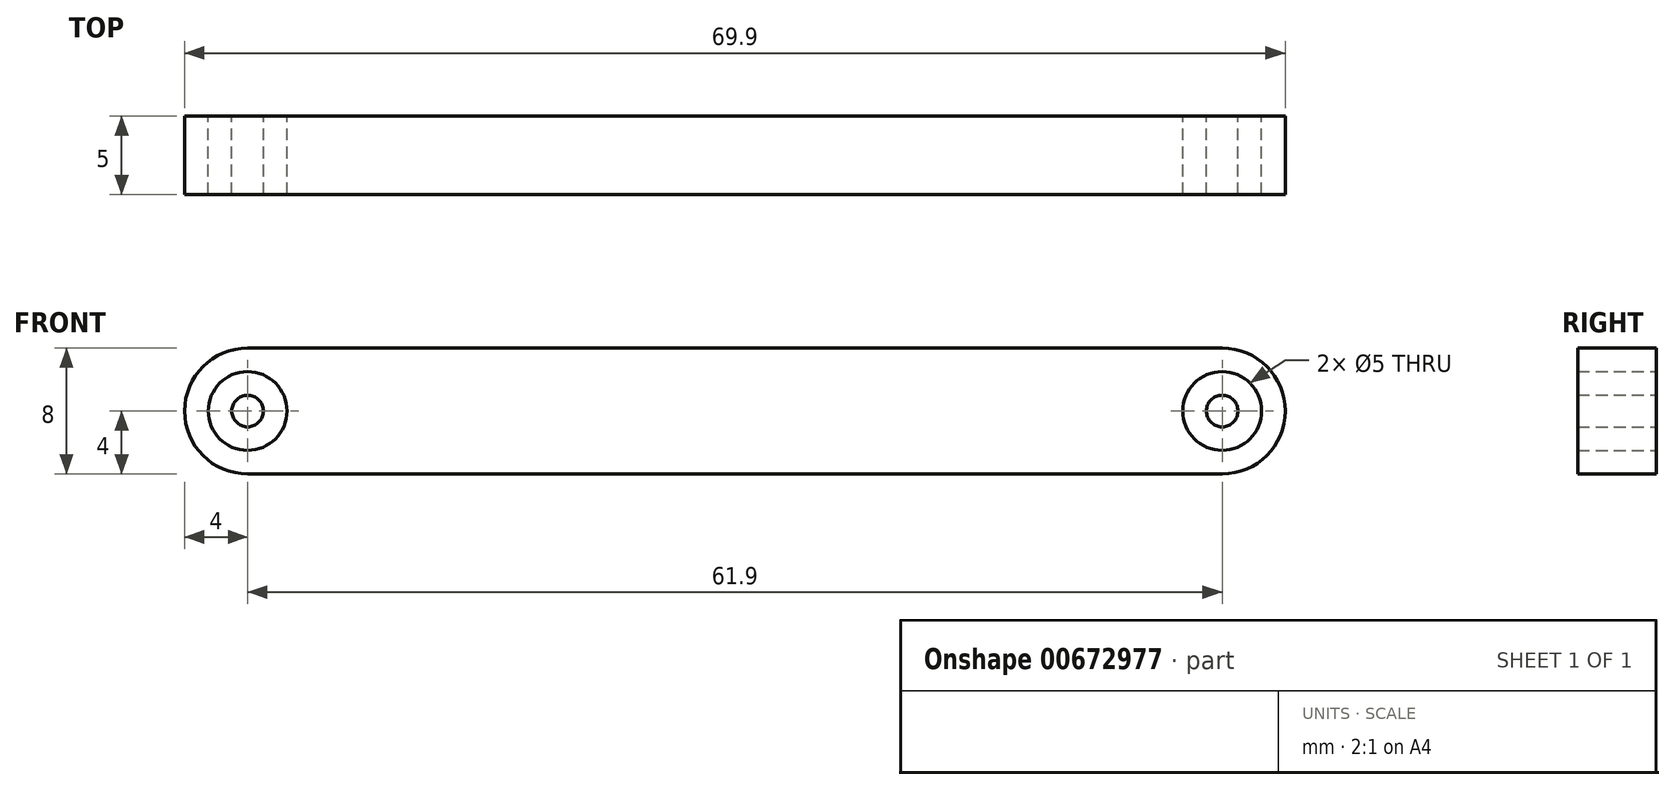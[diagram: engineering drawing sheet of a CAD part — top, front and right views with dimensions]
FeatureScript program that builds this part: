
annotation { "Feature Type Name" : "Feature", "Feature Type Description" : "" }
export const myFeature = defineFeature(function(context is Context, id is Id, definition is map)
    precondition{}
    {
        {
            var Q0;
            Q0=qCreatedBy(makeId("Front.planeOp"),FACE);
            var sketch = newSketch(context, id + "F0", { "sketchPlane" : qUnion([Q0])});
            skCircle(sketch, "E0", {"center": v(61.9, 0) * mm, "radius": 2.5 * mm});
            skCircle(sketch, "E1", {"center": v(61.9, 0) * mm, "radius": 1 * mm});
            skCircle(sketch, "E2", {"center": v(0, 0) * mm, "radius": 2.5 * mm});
            skCircle(sketch, "E3", {"center": v(0, 0) * mm, "radius": 1 * mm});
            skCircle(sketch, "E4", {"center": v(0, 0) * mm, "radius": 4 * mm});
            skCircle(sketch, "E5", {"center": v(61.9, 0) * mm, "radius": 4 * mm});
            skLineSegment(sketch, "E6", {"start": v(61.9, 4) * mm, "end": v(0, 4) * mm});
            skLineSegment(sketch, "E7", {"start": v(0, -4) * mm, "end": v(61.9, -4) * mm});
            skSolve(sketch);
        }
        {
            var Q0;
            Q0 = qSketchRegion(id + "F0", true);
            var Q1;
            Q1=makeQuery(id+"F0.imprint","IMPRINT",FACE,{"disambiguationData":[TD([[makeQuery(id+"F0.imprint","IMPRINT",EDGE,{"derivedFrom":sQuery(id+"F0.wireOp",EDGE,"E3")}),1.0]])]});
            var Q2;
            Q2=makeQuery(id+"F0.imprint","IMPRINT",FACE,{"disambiguationData":[TD([[makeQuery(id+"F0.imprint","IMPRINT",EDGE,{"derivedFrom":sQuery(id+"F0.wireOp",EDGE,"E1")}),1.0]])]});
            extrude(context, id + "F1", {"entities" : qUnion([Q0, Q1, Q2]), "depth" : 5 * mm, "offsetDistance" : 25.4 * mm});
        }
    });
